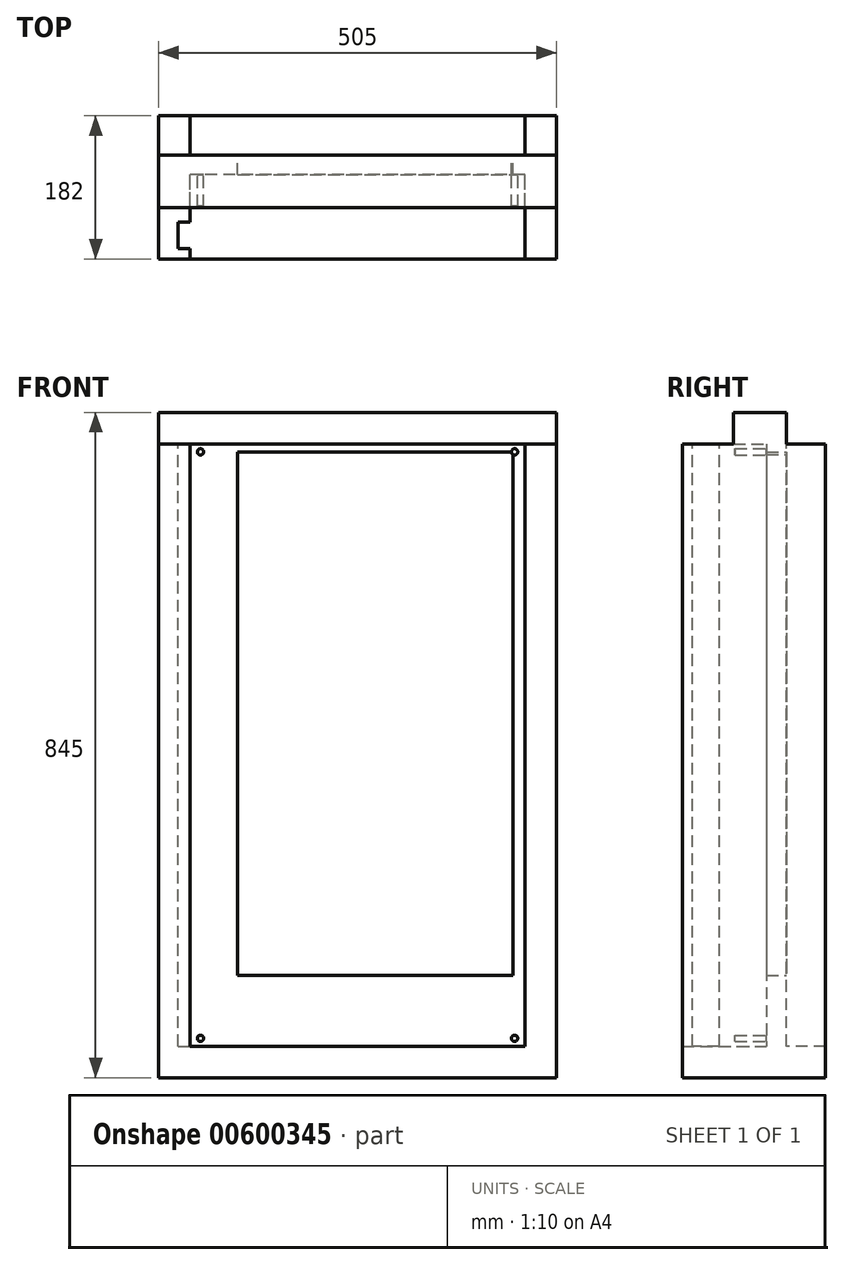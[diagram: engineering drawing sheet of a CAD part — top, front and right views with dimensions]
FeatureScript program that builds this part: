
annotation { "Feature Type Name" : "Feature", "Feature Type Description" : "" }
export const myFeature = defineFeature(function(context is Context, id is Id, definition is map)
    precondition{}
    {
        {
            var Q0;
            Q0=qCreatedBy(makeId("Front.planeOp"),FACE);
            var sketch = newSketch(context, id + "F0", { "sketchPlane" : qUnion([Q0])});
            skLineSegment(sketch, "E0.bottom", {"start": v(0, 0) * mm, "end": v(425, 0) * mm});
            skLineSegment(sketch, "E0.top", {"start": v(0, 765) * mm, "end": v(425, 765) * mm});
            skLineSegment(sketch, "E0.left", {"start": v(0, 0) * mm, "end": v(0, 765) * mm});
            skLineSegment(sketch, "E0.right", {"start": v(425, 0) * mm, "end": v(425, 765) * mm});
            skLineSegment(sketch, "E1.0", {"start": v(0, 755) * mm, "end": v(425, 755) * mm, "construction": true});
            skLineSegment(sketch, "E2.0", {"start": v(13, 0) * mm, "end": v(13, 765) * mm, "construction": true});
            skCircle(sketch, "E3", {"center": v(13, 755) * mm, "radius": 4 * mm});
            skLineSegment(sketch, "E4.0", {"start": v(412, 0) * mm, "end": v(412, 765) * mm, "construction": true});
            skLineSegment(sketch, "E5.0", {"start": v(0, 10) * mm, "end": v(425, 10) * mm, "construction": true});
            skCircle(sketch, "E6", {"center": v(412, 755) * mm, "radius": 4 * mm});
            skCircle(sketch, "E7", {"center": v(412, 10) * mm, "radius": 4 * mm});
            skCircle(sketch, "E8", {"center": v(13, 10) * mm, "radius": 4 * mm});
            skLineSegment(sketch, "E9", {"start": v(465, -40) * mm, "end": v(465, 805) * mm});
            skLineSegment(sketch, "E10", {"start": v(-40, 805) * mm, "end": v(465, 805) * mm});
            skLineSegment(sketch, "E11", {"start": v(-40, 805) * mm, "end": v(-40, -40) * mm});
            skLineSegment(sketch, "E12", {"start": v(-40, -40) * mm, "end": v(465, -40) * mm});
            skLineSegment(sketch, "E13.bottom", {"start": v(60, 755) * mm, "end": v(410, 755) * mm});
            skLineSegment(sketch, "E13.top", {"start": v(60, 90) * mm, "end": v(410, 90) * mm});
            skLineSegment(sketch, "E13.left", {"start": v(60, 755) * mm, "end": v(60, 90) * mm});
            skLineSegment(sketch, "E13.right", {"start": v(410, 755) * mm, "end": v(410, 90) * mm});
            skPoint(sketch, "E13.middle", {"position": v(235, 422.5) * mm});
            skPoint(sketch, "E14", {"position": v(0, 765) * mm});
            skPoint(sketch, "E15", {"position": v(-40, 765) * mm});
            skPoint(sketch, "E16", {"position": v(425, 765) * mm});
            skPoint(sketch, "E17", {"position": v(465, 765) * mm});
            skLineSegment(sketch, "E18", {"start": v(0, 765) * mm, "end": v(-40, 765) * mm});
            skLineSegment(sketch, "E19", {"start": v(425, 765) * mm, "end": v(465, 765) * mm});
            skSolve(sketch);
        }
        {
            var Q0;
            Q0=makeQuery(id+"F0.imprint","IMPRINT",FACE,{"disambiguationData":[TD([[makeQuery(id+"F0.imprint","IMPRINT",EDGE,{"derivedFrom":sQuery(id+"F0.wireOp",EDGE,"E0.bottom")}),-1.0]])]});
            var Q1;
            Q1=makeQuery(id+"F0.imprint","IMPRINT",FACE,{"disambiguationData":[TD([[makeQuery(id+"F0.imprint","IMPRINT",EDGE,{"derivedFrom":sQuery(id+"F0.wireOp",EDGE,"E0.bottom")}),1.0]])]});
            extrude(context, id + "F1", {"entities" : qUnion([Q0, Q1]), "depth" : 25 * mm, "offsetDistance" : 25 * mm});
        }
        {
            var Q0;
            Q0=makeQuery(id+"F0.imprint","IMPRINT",FACE,{"disambiguationData":[TD([[makeQuery(id+"F0.imprint","IMPRINT",EDGE,{"derivedFrom":sQuery(id+"F0.wireOp",EDGE,"E6")}),1.0]])]});
            var Q1;
            Q1=makeQuery(id+"F0.imprint","IMPRINT",FACE,{"disambiguationData":[TD([[makeQuery(id+"F0.imprint","IMPRINT",EDGE,{"derivedFrom":sQuery(id+"F0.wireOp",EDGE,"E3")}),1.0]])]});
            var Q2;
            Q2=makeQuery(id+"F0.imprint","IMPRINT",FACE,{"disambiguationData":[TD([[makeQuery(id+"F0.imprint","IMPRINT",EDGE,{"derivedFrom":sQuery(id+"F0.wireOp",EDGE,"E7")}),1.0]])]});
            var Q3;
            Q3=makeQuery(id+"F0.imprint","IMPRINT",FACE,{"disambiguationData":[TD([[makeQuery(id+"F0.imprint","IMPRINT",EDGE,{"derivedFrom":sQuery(id+"F0.wireOp",EDGE,"E8")}),1.0]])]});
            extrude(context, id + "F2", {"entities" : qUnion([Q0, Q1, Q2, Q3]), "operationType" : NewBodyOperationType.ADD, "depth" : 65 * mm, "offsetDistance" : 25 * mm});
        }
        {
            var Q0;
            Q0=makeQuery(id+"F0.imprint","IMPRINT",FACE,{"disambiguationData":[TD([[makeQuery(id+"F0.imprint","IMPRINT",EDGE,{"derivedFrom":sQuery(id+"F0.wireOp",EDGE,"E0.bottom")}),-1.0]])]});
            var Q1;
            Q1=makeQuery(id+"F2.opExtrude","CAP_FACE",FACE,{"disambiguationData":[OSD([sQuery(id+"F0.wireOp",EDGE,"E8")])],"isStart":false});
            extrude(context, id + "F3", {"entities" : qUnion([Q0]), "operationType" : NewBodyOperationType.ADD, "endBound" : BoundingType.UP_TO_SURFACE, "depth" : 50 * mm, "endBoundEntityFace" : qUnion([Q1]), "offsetDistance" : 25 * mm});
        }
        {
            var Q0;
            Q0=makeQuery(id+"F0.imprint","IMPRINT",FACE,{"disambiguationData":[TD([[makeQuery(id+"F0.imprint","IMPRINT",EDGE,{"derivedFrom":sQuery(id+"F0.wireOp",EDGE,"E0.bottom")}),-1.0]])]});
            extrude(context, id + "F4", {"entities" : qUnion([Q0]), "operationType" : NewBodyOperationType.ADD, "oppositeDirection" : true, "depth" : 50 * mm, "offsetDistance" : 25 * mm});
        }
        {
            var Q0;
            Q0 = qSketchRegion(id + "F0", true);
            var Q1;
            Q1=makeQuery(id+"F3.opExtrude","CAP_FACE",FACE,{"disambiguationData":[OSD([sQuery(id+"F0.wireOp",EDGE,"E0.bottom"),sQuery(id+"F0.wireOp",EDGE,"E0.left"),sQuery(id+"F0.wireOp",EDGE,"E0.right"),sQuery(id+"F0.wireOp",EDGE,"E9"),sQuery(id+"F0.wireOp",EDGE,"E11"),sQuery(id+"F0.wireOp",EDGE,"E12"),sQuery(id+"F0.wireOp",EDGE,"E18"),sQuery(id+"F0.wireOp",EDGE,"E19")])],"isStart":false});
            extrude(context, id + "F5", {"entities" : qUnion([Q0, Q1]), "operationType" : NewBodyOperationType.ADD, "depth" : 67 * mm, "offsetDistance" : 25 * mm});
        }
        {
            var Q0;
            Q0=makeQuery(id+"F5.opExtrude","SWEPT_FACE",FACE,{"disambiguationData":[OSD([sQuery(id+"F0.wireOp",EDGE,"E8"),sQuery(id+"F0.wireOp",EDGE,"E18")])]});
            var sketch = newSketch(context, id + "F6", { "sketchPlane" : qUnion([Q0])});
            skLineSegment(sketch, "E20.bottom", {"start": v(0, -118.85) * mm, "end": v(-15.24, -118.85) * mm});
            skLineSegment(sketch, "E20.top", {"start": v(0, -84.94) * mm, "end": v(-15.24, -84.94) * mm});
            skLineSegment(sketch, "E20.left", {"start": v(0, -118.85) * mm, "end": v(0, -84.94) * mm});
            skLineSegment(sketch, "E20.right", {"start": v(-15.24, -118.85) * mm, "end": v(-15.24, -84.94) * mm});
            skSolve(sketch);
        }
        {
            var Q0;
            Q0 = qSketchRegion(id + "F6", true);
            var Q1;
            {var subQ0=sQuery(id+"F0.wireOp",EDGE,"E0.bottom");Q1=makeQuery(id+"F5.boolean.opBoolean","MERGE",FACE,{"derivedFrom":[makeQuery(id+"F3.opExtrude","SWEPT_FACE",FACE,{"disambiguationData":[OSD([subQ0])]}),makeQuery(id+"F5.opExtrude","SWEPT_FACE",FACE,{"disambiguationData":[OSD([subQ0]),TDD([makeQuery(id+"F0.imprint","IMPRINT",EDGE,{"derivedFrom":subQ0})])]}),makeQuery(id+"F5.opExtrude","SWEPT_FACE",FACE,{"disambiguationData":[OSD([subQ0]),TDD([makeQuery(id+"F3.opExtrude","CAP_EDGE",EDGE,{"disambiguationData":[OSD([subQ0])],"isStart":false})])]})]});}
            extrude(context, id + "F7", {"entities" : qUnion([Q0]), "operationType" : NewBodyOperationType.REMOVE, "endBound" : BoundingType.UP_TO_SURFACE, "oppositeDirection" : true, "depth" : 25 * mm, "endBoundEntityFace" : qUnion([Q1]), "offsetDistance" : 25 * mm});
        }
    });
